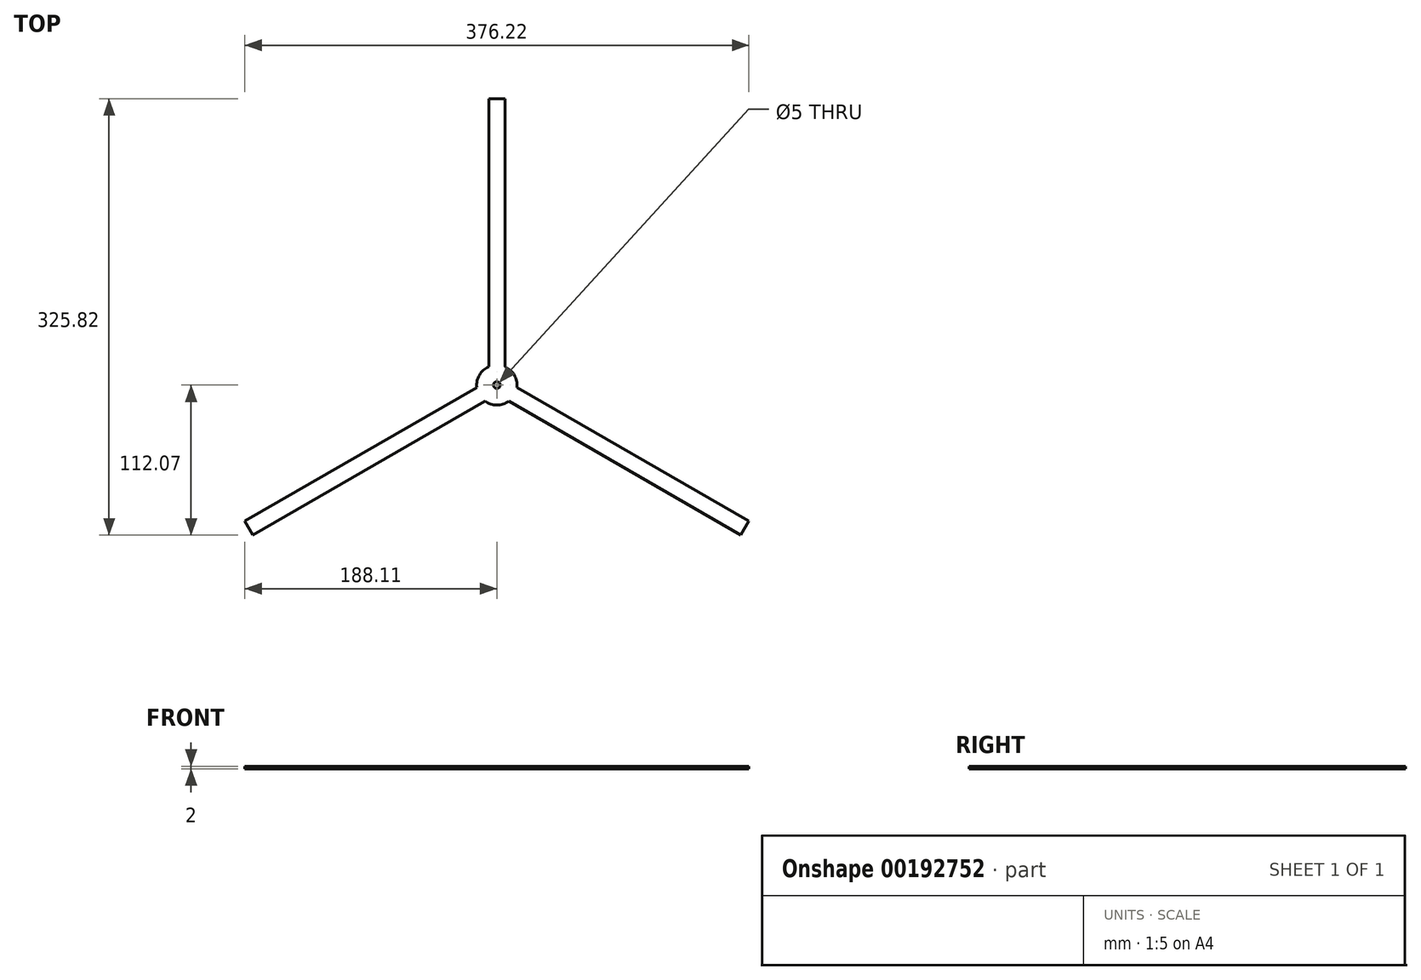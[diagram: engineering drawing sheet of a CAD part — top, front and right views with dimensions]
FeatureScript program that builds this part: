
annotation { "Feature Type Name" : "Feature", "Feature Type Description" : "" }
export const myFeature = defineFeature(function(context is Context, id is Id, definition is map)
    precondition{}
    {
        {
            var Q0;
            Q0=qCreatedBy(makeId("Top.planeOp"),FACE);
            var sketch = newSketch(context, id + "F0", { "sketchPlane" : qUnion([Q0])});
            skCircle(sketch, "E0", {"center": v(0, 0) * mm, "radius": 15 * mm});
            skLineSegment(sketch, "E1", {"start": v(0, 0) * mm, "end": v(0, 15) * mm, "construction": true});
            skLineSegment(sketch, "E2", {"start": v(0, 213.75) * mm, "end": v(-6, 213.75) * mm});
            skLineSegment(sketch, "E3", {"start": v(-6, 213.75) * mm, "end": v(-6, 13.75) * mm});
            skLineSegment(sketch, "E4.MirrorCS", {"start": v(0, 213.75) * mm, "end": v(6, 213.75) * mm});
            skLineSegment(sketch, "E5.MirrorCS", {"start": v(6, 213.75) * mm, "end": v(6, 13.75) * mm});
            skLineSegment(sketch, "E6.1.0", {"start": v(-185.11, -106.87) * mm, "end": v(-182.11, -112.07) * mm});
            skLineSegment(sketch, "E6.1.1", {"start": v(-185.11, -106.87) * mm, "end": v(-188.11, -101.68) * mm});
            skLineSegment(sketch, "E6.1.2", {"start": v(-188.11, -101.68) * mm, "end": v(-14.9, -1.68) * mm});
            skLineSegment(sketch, "E6.1.3", {"start": v(-182.11, -112.07) * mm, "end": v(-8.9, -12.07) * mm});
            skLineSegment(sketch, "E6.2.0", {"start": v(185.11, -106.87) * mm, "end": v(188.11, -101.68) * mm});
            skLineSegment(sketch, "E6.2.1", {"start": v(185.11, -106.87) * mm, "end": v(182.11, -112.07) * mm});
            skLineSegment(sketch, "E6.2.2", {"start": v(182.11, -112.07) * mm, "end": v(8.9, -12.07) * mm});
            skLineSegment(sketch, "E6.2.3", {"start": v(188.11, -101.68) * mm, "end": v(14.9, -1.68) * mm});
            skSolve(sketch);
        }
        {
            var Q0;
            {var subQ0=sQuery(id+"F0.wireOp",EDGE,"E0");var subQ4=makeQuery(id+"F0.imprint","INTERSECT",VERTEX,{"derivedFrom":[subQ0,sQuery(id+"F0.wireOp",EDGE,"E3")]});Q0=makeQuery(id+"F0.imprint","IMPRINT",FACE,{"disambiguationData":[TD([[makeQuery(id+"F0.imprint","IMPRINT",EDGE,{"disambiguationData":[TD([[subQ4,1.0]])],"derivedFrom":subQ0}),1.0]])]});}
            var Q1;
            Q1=makeQuery(id+"F0.imprint","IMPRINT",FACE,{"disambiguationData":[TD([[makeQuery(id+"F0.imprint","IMPRINT",EDGE,{"derivedFrom":sQuery(id+"F0.wireOp",EDGE,"E6.1.0")}),1.0]])]});
            var Q2;
            Q2=makeQuery(id+"F0.imprint","IMPRINT",FACE,{"disambiguationData":[TD([[makeQuery(id+"F0.imprint","IMPRINT",EDGE,{"derivedFrom":sQuery(id+"F0.wireOp",EDGE,"E2")}),1.0]])]});
            var Q3;
            Q3=makeQuery(id+"F0.imprint","IMPRINT",FACE,{"disambiguationData":[TD([[makeQuery(id+"F0.imprint","IMPRINT",EDGE,{"derivedFrom":sQuery(id+"F0.wireOp",EDGE,"E6.2.0")}),1.0]])]});
            extrude(context, id + "F1", {"entities" : qUnion([Q0, Q1, Q2, Q3]), "depth" : 2 * mm});
        }
        {
            var Q0;
            Q0=makeQuery(id+"F1.opExtrude","CAP_FACE",FACE,{"disambiguationData":[OSD([sQuery(id+"F0.wireOp",EDGE,"E0"),sQuery(id+"F0.wireOp",EDGE,"E2"),sQuery(id+"F0.wireOp",EDGE,"E3"),sQuery(id+"F0.wireOp",EDGE,"E4.MirrorCS"),sQuery(id+"F0.wireOp",EDGE,"E5.MirrorCS"),sQuery(id+"F0.wireOp",EDGE,"E6.1.0"),sQuery(id+"F0.wireOp",EDGE,"E6.1.1"),sQuery(id+"F0.wireOp",EDGE,"E6.1.2"),sQuery(id+"F0.wireOp",EDGE,"E6.1.3"),sQuery(id+"F0.wireOp",EDGE,"E6.2.0"),sQuery(id+"F0.wireOp",EDGE,"E6.2.1"),sQuery(id+"F0.wireOp",EDGE,"E6.2.2"),sQuery(id+"F0.wireOp",EDGE,"E6.2.3")])],"isStart":false});
            var sketch = newSketch(context, id + "F2", { "sketchPlane" : qUnion([Q0])});
            skCircle(sketch, "E7", {"center": v(0, 0) * mm, "radius": 2.5 * mm});
            skSolve(sketch);
        }
        {
            var Q0;
            Q0=makeQuery(id+"F2.imprint","IMPRINT",FACE,{"disambiguationData":[TD([[makeQuery(id+"F2.imprint","IMPRINT",EDGE,{"derivedFrom":sQuery(id+"F2.wireOp",EDGE,"E7")}),1.0]])]});
            extrude(context, id + "F3", {"entities" : qUnion([Q0]), "operationType" : NewBodyOperationType.REMOVE, "oppositeDirection" : true, "depth" : 25 * mm});
        }
    });
